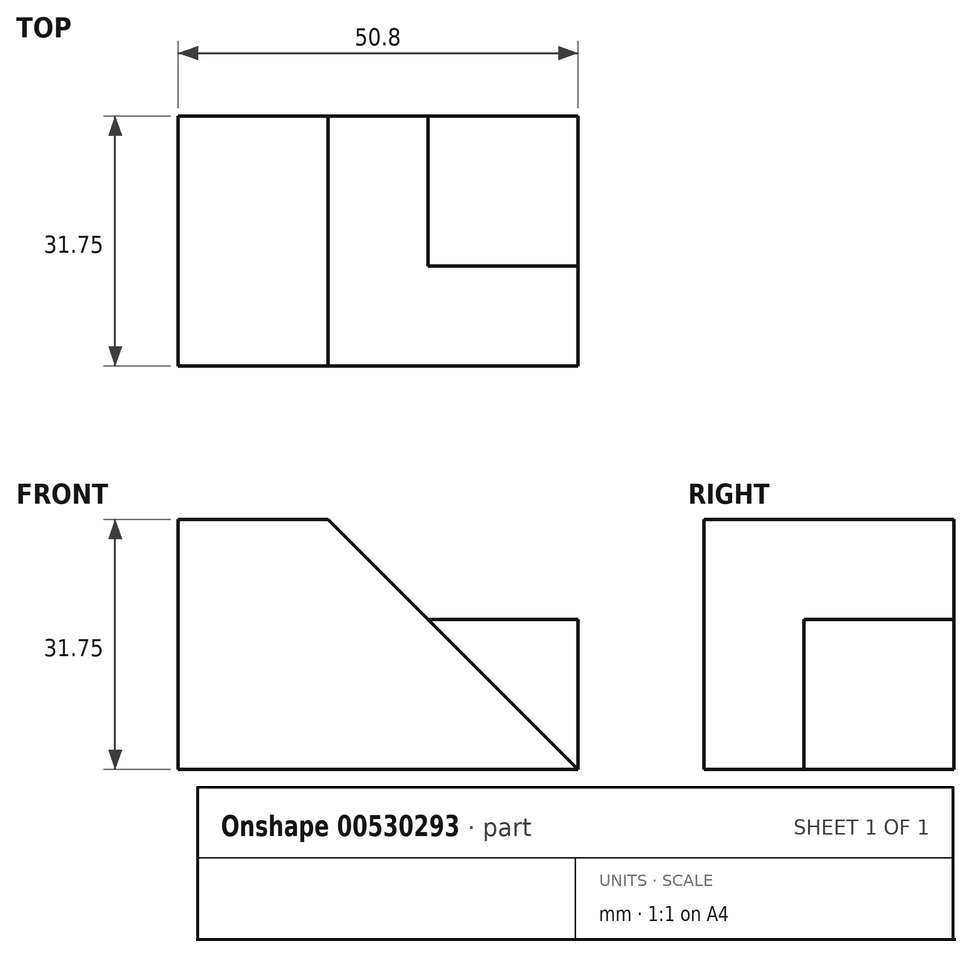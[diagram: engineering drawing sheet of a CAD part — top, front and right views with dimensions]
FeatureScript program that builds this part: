
annotation { "Feature Type Name" : "Feature", "Feature Type Description" : "" }
export const myFeature = defineFeature(function(context is Context, id is Id, definition is map)
    precondition{}
    {
        {
            var Q0;
            Q0=qCreatedBy(makeId("Front.planeOp"),FACE);
            var sketch = newSketch(context, id + "F0", { "sketchPlane" : qUnion([Q0])});
            skLineSegment(sketch, "E0", {"start": v(-29.57, 31.75) * mm, "end": v(-29.57, 0) * mm});
            skLineSegment(sketch, "E1", {"start": v(-29.57, 0) * mm, "end": v(21.23, 0) * mm});
            skLineSegment(sketch, "E2", {"start": v(21.23, 0) * mm, "end": v(21.23, 31.75) * mm});
            skLineSegment(sketch, "E3", {"start": v(21.23, 31.75) * mm, "end": v(-29.57, 31.75) * mm});
            skSolve(sketch);
        }
        {
            var Q0;
            Q0=makeQuery(id+"F0.imprint","IMPRINT",FACE,{"disambiguationData":[TD([[makeQuery(id+"F0.imprint","IMPRINT",EDGE,{"derivedFrom":sQuery(id+"F0.wireOp",EDGE,"E0")}),1.0]])]});
            extrude(context, id + "F1", {"entities" : qUnion([Q0]), "depth" : 31.75 * mm, "offsetDistance" : 25.4 * mm});
        }
        {
            var Q0;
            Q0=makeQuery(id+"F1.opExtrude","CAP_FACE",FACE,{"disambiguationData":[OSD([sQuery(id+"F0.wireOp",EDGE,"E0"),sQuery(id+"F0.wireOp",EDGE,"E1"),sQuery(id+"F0.wireOp",EDGE,"E2"),sQuery(id+"F0.wireOp",EDGE,"E3")])],"isStart":false});
            var sketch = newSketch(context, id + "F2", { "sketchPlane" : qUnion([Q0])});
            skLineSegment(sketch, "E4", {"start": v(-10.52, 31.75) * mm, "end": v(21.23, 0) * mm});
            skSolve(sketch);
        }
        {
            var Q0;
            {var subQ0=sQuery(id+"F2.wireOp",EDGE,"E4");Q0=makeQuery(id+"F2.imprint","IMPRINT",FACE,{"disambiguationData":[TD([[makeQuery(id+"F2.imprint","IMPRINT",EDGE,{"derivedFrom":subQ0}),1.0]])]});}
            extrude(context, id + "F3", {"entities" : qUnion([Q0]), "operationType" : NewBodyOperationType.REMOVE, "oppositeDirection" : true, "depth" : 12.7 * mm, "offsetDistance" : 25.4 * mm});
        }
        {
            var Q0;
            Q0=makeQuery(id+"F1.opExtrude","CAP_FACE",FACE,{"disambiguationData":[OSD([sQuery(id+"F0.wireOp",EDGE,"E0"),sQuery(id+"F0.wireOp",EDGE,"E1"),sQuery(id+"F0.wireOp",EDGE,"E2"),sQuery(id+"F0.wireOp",EDGE,"E3")])],"isStart":true});
            var sketch = newSketch(context, id + "F4", { "sketchPlane" : qUnion([Q0])});
            skLineSegment(sketch, "E5", {"start": v(10.52, 31.75) * mm, "end": v(-2.18, 19.05) * mm});
            skLineSegment(sketch, "E6", {"start": v(-2.18, 19.05) * mm, "end": v(-21.23, 19.05) * mm});
            skSolve(sketch);
        }
        {
            var Q0;
            {var subQ0=sQuery(id+"F4.wireOp",EDGE,"E5");Q0=makeQuery(id+"F4.imprint","IMPRINT",FACE,{"disambiguationData":[TD([[makeQuery(id+"F4.imprint","IMPRINT",EDGE,{"derivedFrom":subQ0}),-1.0]])]});}
            extrude(context, id + "F5", {"entities" : qUnion([Q0]), "operationType" : NewBodyOperationType.REMOVE, "oppositeDirection" : true, "depth" : 19.05 * mm, "offsetDistance" : 25.4 * mm});
        }
    });
